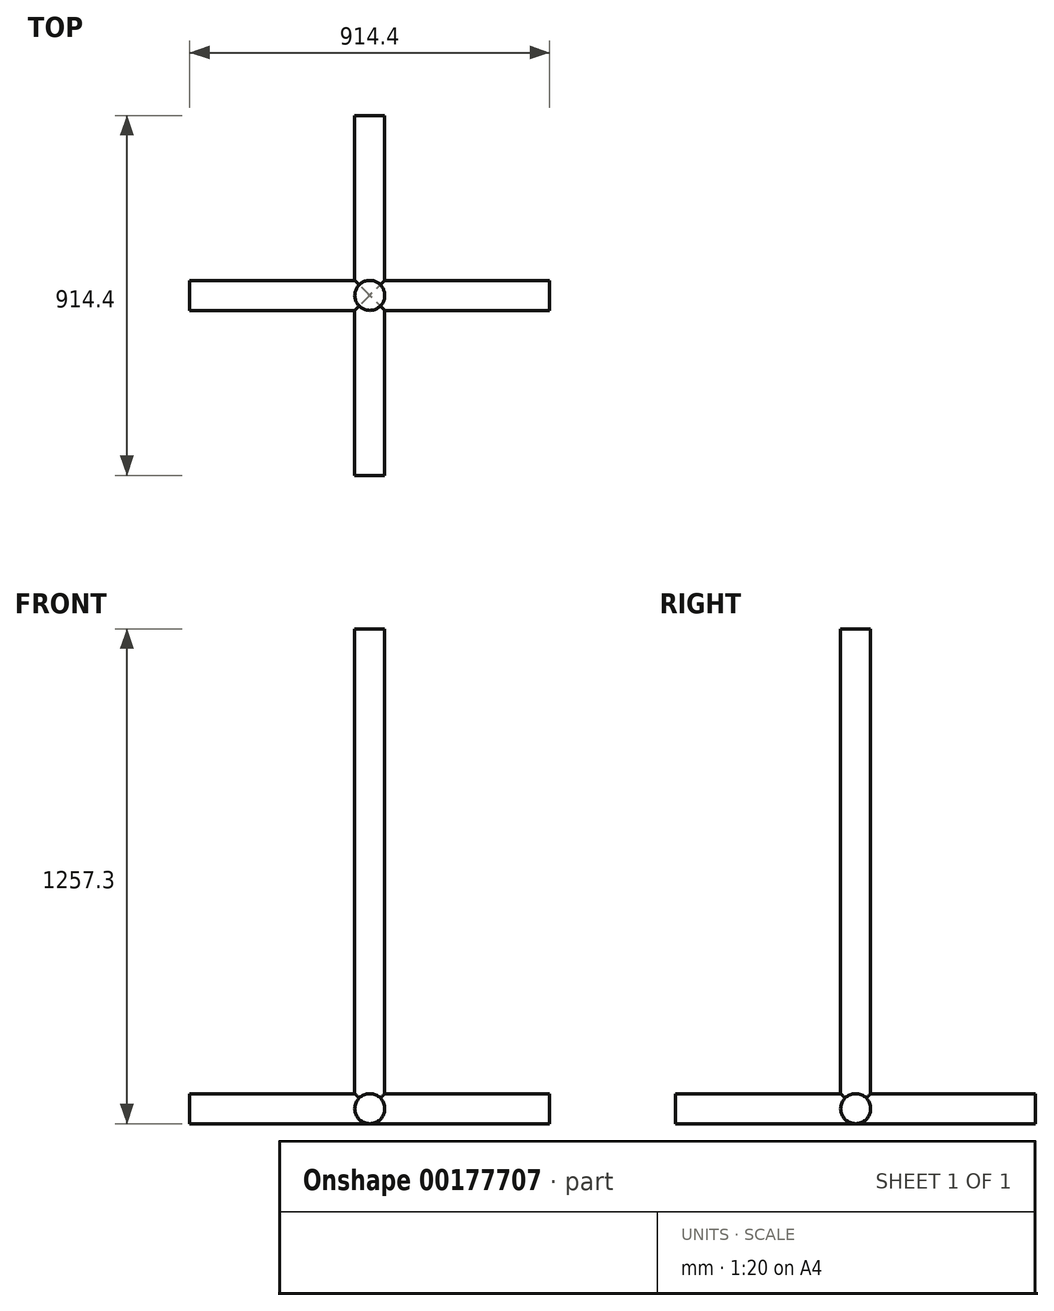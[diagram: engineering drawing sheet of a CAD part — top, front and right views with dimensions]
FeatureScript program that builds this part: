
annotation { "Feature Type Name" : "Feature", "Feature Type Description" : "" }
export const myFeature = defineFeature(function(context is Context, id is Id, definition is map)
    precondition{}
    {
        {
            var Q0;
            Q0=qCreatedBy(makeId("Front.planeOp"),FACE);
            var sketch = newSketch(context, id + "F0", { "sketchPlane" : qUnion([Q0])});
            skCircle(sketch, "E0", {"center": v(0, 0) * mm, "radius": 38.1 * mm});
            skSolve(sketch);
        }
        {
            var Q0;
            Q0=makeQuery(id+"F0.imprint","IMPRINT",FACE,{"disambiguationData":[TD([[makeQuery(id+"F0.imprint","IMPRINT",EDGE,{"derivedFrom":sQuery(id+"F0.wireOp",EDGE,"E0")}),1.0]])]});
            extrude(context, id + "F1", {"entities" : qUnion([Q0]), "endBound" : BoundingType.SYMMETRIC, "depth" : 914.4 * mm});
        }
        {
            var Q0;
            Q0=qCreatedBy(makeId("Right.planeOp"),FACE);
            var sketch = newSketch(context, id + "F2", { "sketchPlane" : qUnion([Q0])});
            skCircle(sketch, "E1", {"center": v(0, 0) * mm, "radius": 38.1 * mm});
            skSolve(sketch);
        }
        {
            var Q0;
            Q0 = qSketchRegion(id + "F2", true);
            extrude(context, id + "F3", {"entities" : qUnion([Q0]), "operationType" : NewBodyOperationType.ADD, "endBound" : BoundingType.SYMMETRIC, "depth" : 914.4 * mm});
        }
        {
            var Q0;
            Q0=qCreatedBy(makeId("Top.planeOp"),FACE);
            var sketch = newSketch(context, id + "F4", { "sketchPlane" : qUnion([Q0])});
            skCircle(sketch, "E2", {"center": v(0, 0) * mm, "radius": 38.1 * mm});
            skSolve(sketch);
        }
        {
            var Q0;
            Q0 = qSketchRegion(id + "F4", true);
            extrude(context, id + "F5", {"entities" : qUnion([Q0]), "operationType" : NewBodyOperationType.ADD, "depth" : 1219.2 * mm});
        }
    });
